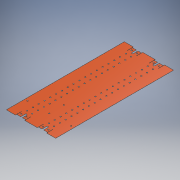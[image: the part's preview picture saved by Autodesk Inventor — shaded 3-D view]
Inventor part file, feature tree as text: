
AUTODESK INVENTOR PART (.ipt)
format: ipt  version: 2019 (Build 230136000, 136)  size: 377,344 bytes
history: native  units: mm
features: mirror x5, extrude x4, other x4
ambient origin geometry x8: Origin, YZ Plane, XZ Plane, XY Plane, X Axis, Y Axis, Z Axis, Center Point
bodies: Solid1 (feature_tree)
feature tree (13):
  extrude  "Skin Body"  Depth=1294.0mm
  extrude  "Feature Cut"  Depth=647.0mm
  mirror  "Feature Cut Side Mirror"
  mirror  "Feature Cut Mirror"
  extrude  "End Cut"  Depth=424.0mm
  mirror  "End Cut Mirror"
  extrude  "Slot Cut"  Depth=212.0mm
  mirror  "Slot Cut Side Mirror"
  mirror  "Slot Cut Mirror"
  other  "Skin Scheme"
  other  "Feature Cut Outline"
  other  "End Cut Outline"
  other  "Slot Cut Outline"
